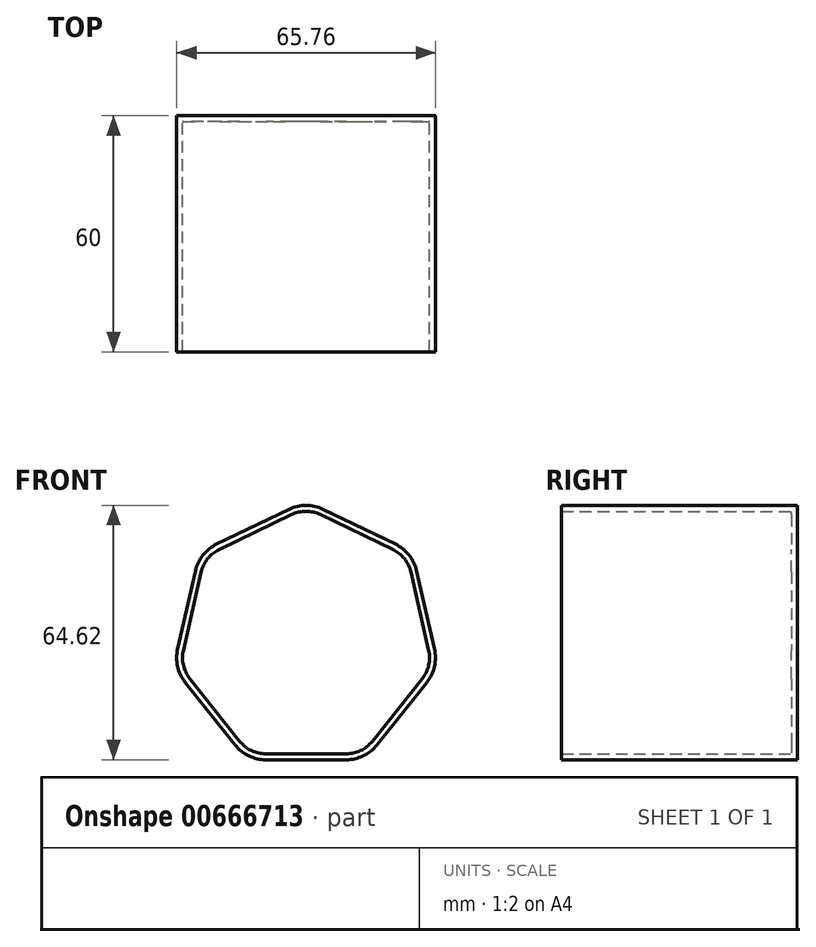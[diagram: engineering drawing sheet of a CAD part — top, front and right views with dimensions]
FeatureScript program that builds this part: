
annotation { "Feature Type Name" : "Feature", "Feature Type Description" : "" }
export const myFeature = defineFeature(function(context is Context, id is Id, definition is map)
    precondition{}
    {
        {
            var Q0;
            Q0=qCreatedBy(makeId("Front.planeOp"),FACE);
            var sketch = newSketch(context, id + "F0", { "sketchPlane" : qUnion([Q0])});
            skCircle(sketch, "E0.cCircle", {"center": v(0, 0) * mm, "radius": 34.57 * mm, "construction": true});
            skLineSegment(sketch, "E0.0", {"start": v(4.34, 32.48) * mm, "end": v(22.7, 23.64) * mm});
            skLineSegment(sketch, "E0.1", {"start": v(28.1, 16.86) * mm, "end": v(32.63, -3) * mm});
            skLineSegment(sketch, "E0.2", {"start": v(30.7, -11.46) * mm, "end": v(18, -27.38) * mm});
            skLineSegment(sketch, "E0.3", {"start": v(10.18, -31.15) * mm, "end": v(-10.18, -31.15) * mm});
            skLineSegment(sketch, "E0.4", {"start": v(-18, -27.38) * mm, "end": v(-30.7, -11.46) * mm});
            skLineSegment(sketch, "E0.5", {"start": v(-32.63, -3) * mm, "end": v(-28.1, 16.86) * mm});
            skLineSegment(sketch, "E0.6", {"start": v(-22.7, 23.64) * mm, "end": v(-4.34, 32.48) * mm});
            skPoint(sketch, "E1.visualSharp", {"position": v(0, 34.57) * mm});
            skArc(sketch, "E1.filletArc", {"start": v(4.34, 32.48) * mm, "mid": v(0, 33.47) * mm, "end": v(-4.34, 32.48) * mm});
            skPoint(sketch, "E2.visualSharp", {"position": v(27.03, 21.55) * mm});
            skArc(sketch, "E2.filletArc", {"start": v(28.1, 16.86) * mm, "mid": v(26.17, 20.87) * mm, "end": v(22.7, 23.64) * mm});
            skPoint(sketch, "E3.visualSharp", {"position": v(33.7, -7.7) * mm});
            skArc(sketch, "E3.filletArc", {"start": v(30.7, -11.46) * mm, "mid": v(32.63, -7.45) * mm, "end": v(32.63, -3) * mm});
            skPoint(sketch, "E4.visualSharp", {"position": v(15, -31.15) * mm});
            skArc(sketch, "E4.filletArc", {"start": v(10.18, -31.15) * mm, "mid": v(14.52, -30.16) * mm, "end": v(18, -27.38) * mm});
            skPoint(sketch, "E5.visualSharp", {"position": v(-15, -31.15) * mm});
            skArc(sketch, "E5.filletArc", {"start": v(-18, -27.38) * mm, "mid": v(-14.52, -30.16) * mm, "end": v(-10.18, -31.15) * mm});
            skPoint(sketch, "E6.visualSharp", {"position": v(-33.7, -7.7) * mm});
            skArc(sketch, "E6.filletArc", {"start": v(-32.63, -3) * mm, "mid": v(-32.63, -7.45) * mm, "end": v(-30.7, -11.46) * mm});
            skPoint(sketch, "E7.visualSharp", {"position": v(-27.03, 21.55) * mm});
            skArc(sketch, "E7.filletArc", {"start": v(-22.7, 23.64) * mm, "mid": v(-26.17, 20.87) * mm, "end": v(-28.1, 16.86) * mm});
            skSolve(sketch);
        }
        {
            var Q0;
            Q0=makeQuery(id+"F0.imprint","IMPRINT",FACE,{"disambiguationData":[TD([[makeQuery(id+"F0.imprint","IMPRINT",EDGE,{"derivedFrom":sQuery(id+"F0.wireOp",EDGE,"E0.0")}),-1.0]])]});
            extrude(context, id + "F1", {"entities" : qUnion([Q0]), "depth" : 60 * mm, "offsetDistance" : 25 * mm});
        }
        {
            var Q0;
            Q0=makeQuery(id+"F1.opExtrude","CAP_FACE",FACE,{"disambiguationData":[OSD([sQuery(id+"F0.wireOp",EDGE,"E0.0"),sQuery(id+"F0.wireOp",EDGE,"E0.1"),sQuery(id+"F0.wireOp",EDGE,"E0.2"),sQuery(id+"F0.wireOp",EDGE,"E0.3"),sQuery(id+"F0.wireOp",EDGE,"E0.4"),sQuery(id+"F0.wireOp",EDGE,"E0.5"),sQuery(id+"F0.wireOp",EDGE,"E0.6"),sQuery(id+"F0.wireOp",EDGE,"E1.filletArc"),sQuery(id+"F0.wireOp",EDGE,"E2.filletArc"),sQuery(id+"F0.wireOp",EDGE,"E3.filletArc"),sQuery(id+"F0.wireOp",EDGE,"E4.filletArc"),sQuery(id+"F0.wireOp",EDGE,"E5.filletArc"),sQuery(id+"F0.wireOp",EDGE,"E6.filletArc"),sQuery(id+"F0.wireOp",EDGE,"E7.filletArc")])],"isStart":false});
            shell(context, id + "F2", {"entities" : qUnion([Q0]), "thickness" : 1.5 * mm});
        }
    });
